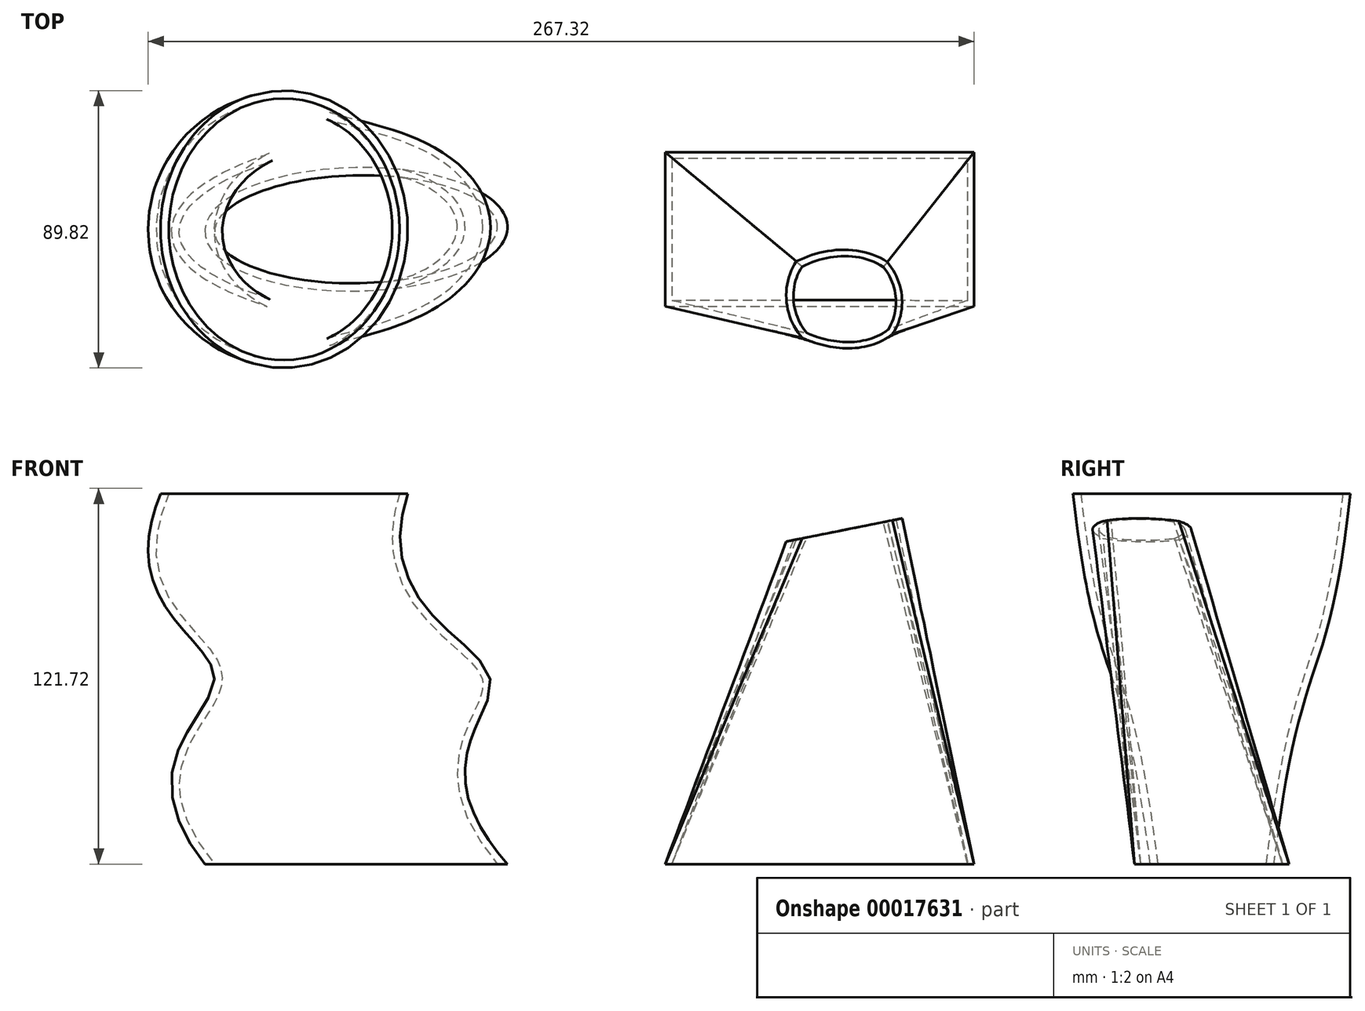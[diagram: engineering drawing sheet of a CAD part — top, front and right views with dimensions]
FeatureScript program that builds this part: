
annotation { "Feature Type Name" : "Feature", "Feature Type Description" : "" }
export const myFeature = defineFeature(function(context is Context, id is Id, definition is map)
    precondition{}
    {
        {
            var Q0;
            Q0=qCreatedBy(makeId("Top.planeOp"),FACE);
            var sketch = newSketch(context, id + "F0", { "sketchPlane" : qUnion([Q0])});
            skLineSegment(sketch, "E0.rect.bottom", {"start": v(-50, 25) * mm, "end": v(50, 25) * mm});
            skLineSegment(sketch, "E0.rect.top", {"start": v(-50, -25) * mm, "end": v(50, -25) * mm});
            skLineSegment(sketch, "E0.rect.left", {"start": v(-50, 25) * mm, "end": v(-50, -25) * mm});
            skLineSegment(sketch, "E0.rect.right", {"start": v(50, 25) * mm, "end": v(50, -25) * mm});
            skPoint(sketch, "E0.rect.middle", {"position": v(0, 0) * mm});
            skSolve(sketch);
        }
        {
            var Q0;
            Q0=qCreatedBy(makeId("Top.planeOp"),FACE);
            cPlane(context, id + "F1", {"entities" : qUnion([Q0]), "cplaneType" : CPlaneType.OFFSET, "offset" : 120 * mm, "width" : 150 * mm, "height" : 150 * mm});
        }
        {
            var Q0;
            Q0=qCreatedBy(id+"F1.planeOp",FACE);
            var sketch = newSketch(context, id + "F2", { "sketchPlane" : qUnion([Q0])});
            skCircle(sketch, "E1", {"center": v(10, -25) * mm, "radius": 15 * mm});
            skSolve(sketch);
        }
        {
            var Q0;
            Q0=makeQuery(id+"F0.imprint","IMPRINT",FACE,{"disambiguationData":[TD([[makeQuery(id+"F0.imprint","IMPRINT",EDGE,{"derivedFrom":sQuery(id+"F0.wireOp",EDGE,"E0.rect.bottom")}),-1.0]])]});
            var Q1;
            Q1=makeQuery(id+"F2.imprint","IMPRINT",FACE,{"disambiguationData":[TD([[makeQuery(id+"F2.imprint","IMPRINT",EDGE,{"derivedFrom":sQuery(id+"F2.wireOp",EDGE,"E1")}),1.0]])]});
            loft(context, id + "F3", {"sheetProfilesArray" : [{ "sheetProfileEntities" : qUnion([Q0]) }, { "sheetProfileEntities" : qUnion([Q1]) }]});
        }
        {
            var Q0;
            Q0=makeQuery(id+"F3.opLoft","CAP_FACE",FACE,{"disambiguationData":[OSD([makeQuery(id+"F0.imprint","IMPRINT",FACE,{"disambiguationData":[TD([[makeQuery(id+"F0.imprint","IMPRINT",EDGE,{"derivedFrom":sQuery(id+"F0.wireOp",EDGE,"E0.rect.bottom")}),-1.0]])]})])],"isStart":true});
            var Q1;
            Q1=makeQuery(id+"F3.opLoft","CAP_FACE",FACE,{"disambiguationData":[OSD([makeQuery(id+"F2.imprint","IMPRINT",FACE,{"disambiguationData":[TD([[makeQuery(id+"F2.imprint","IMPRINT",EDGE,{"derivedFrom":sQuery(id+"F2.wireOp",EDGE,"E1")}),1.0]])]})])],"isStart":true});
            shell(context, id + "F4", {"entities" : qUnion([Q0, Q1]), "thickness" : 2 * mm});
        }
        {
            var Q0;
            Q0=qCreatedBy(makeId("Front.planeOp"),FACE);
            var sketch = newSketch(context, id + "F5", { "sketchPlane" : qUnion([Q0])});
            skFitSpline(sketch, "E2", {"points": [v(-198.97, 0) * mm, v(-195.86, 60.6) * mm, v(-213.34, 120) * mm], "startDerivative": vector(-159.17, 200) * mm, "endDerivative": vector(89.09, 218.52) * mm});
            skSolve(sketch);
        }
        {
            var Q0;
            Q0=qCreatedBy(makeId("Top.planeOp"),FACE);
            var sketch = newSketch(context, id + "F6", { "sketchPlane" : qUnion([Q0])});
            skEllipse(sketch, "E3", {"center": v(-150, 0) * mm, "majorRadius": 49.01 * mm, "minorRadius": 20 * mm, "majorAxis": v(-1, -0.02)});
            skSolve(sketch);
        }
        {
            var Q0;
            Q0=qCreatedBy(id+"F1.planeOp",FACE);
            var sketch = newSketch(context, id + "F7", { "sketchPlane" : qUnion([Q0])});
            skEllipse(sketch, "E4", {"center": v(-173.34, 0) * mm, "majorRadius": 40 * mm, "minorRadius": 44.9 * mm, "majorAxis": v(-1, 0)});
            skSolve(sketch);
        }
        {
            var Q0;
            Q0=makeQuery(id+"F6.imprint","IMPRINT",FACE,{"disambiguationData":[TD([[makeQuery(id+"F6.imprint","IMPRINT",EDGE,{"derivedFrom":sQuery(id+"F6.wireOp",EDGE,"E3")}),1.0]])]});
            var Q1;
            Q1=makeQuery(id+"F7.imprint","IMPRINT",FACE,{"disambiguationData":[TD([[makeQuery(id+"F7.imprint","IMPRINT",EDGE,{"derivedFrom":sQuery(id+"F7.wireOp",EDGE,"E4")}),1.0]])]});
            var Q2;
            Q2=sQuery(id+"F5.wireOp",EDGE,"E2");
            loft(context, id + "F8", {"addGuides" : true, "sheetProfilesArray" : [{ "sheetProfileEntities" : qUnion([Q0]) }, { "sheetProfileEntities" : qUnion([Q1]) }], "guidesArray" : [{ "guideEntities" : qUnion([Q2]), "guideDerivativeType" : LoftGuideDerivativeType.DEFAULT, "guideDerivativeMagnitude" : 1 }]});
        }
        {
            var Q0;
            Q0=makeQuery(id+"F8.opLoft","CAP_FACE",FACE,{"disambiguationData":[OSD([makeQuery(id+"F7.imprint","IMPRINT",FACE,{"disambiguationData":[TD([[makeQuery(id+"F7.imprint","IMPRINT",EDGE,{"derivedFrom":sQuery(id+"F7.wireOp",EDGE,"E4")}),1.0]])]})])],"isStart":true});
            var Q1;
            Q1=makeQuery(id+"F8.opLoft","CAP_FACE",FACE,{"disambiguationData":[OSD([makeQuery(id+"F6.imprint","IMPRINT",FACE,{"disambiguationData":[TD([[makeQuery(id+"F6.imprint","IMPRINT",EDGE,{"derivedFrom":sQuery(id+"F6.wireOp",EDGE,"E3")}),1.0]])]})])],"isStart":true});
            shell(context, id + "F9", {"entities" : qUnion([Q0, Q1]), "thickness" : 2.5 * mm});
        }
        {
            var Q0;
            Q0=qCreatedBy(makeId("Front.planeOp"),FACE);
            var sketch = newSketch(context, id + "F11", { "sketchPlane" : qUnion([Q0])});
            skLineSegment(sketch, "E5", {"start": v(-14.2, 103.8) * mm, "end": v(34.77, 113.6) * mm});
            skLineSegment(sketch, "E6", {"start": v(34.77, 113.6) * mm, "end": v(34.77, 121.94) * mm});
            skLineSegment(sketch, "E7", {"start": v(34.77, 121.94) * mm, "end": v(-16.03, 121.8) * mm});
            skLineSegment(sketch, "E8", {"start": v(-16.03, 121.8) * mm, "end": v(-14.2, 103.8) * mm});
            skSolve(sketch);
        }
        {
            var Q0;
            Q0=makeQuery(id+"F11.imprint","IMPRINT",FACE,{"disambiguationData":[TD([[makeQuery(id+"F11.imprint","IMPRINT",EDGE,{"derivedFrom":sQuery(id+"F11.wireOp",EDGE,"E5")}),1.0]])]});
            extrude(context, id + "F10", {"entities" : qUnion([Q0]), "operationType" : NewBodyOperationType.REMOVE, "endBound" : BoundingType.THROUGH_ALL, "depth" : 25 * mm});
        }
    });
